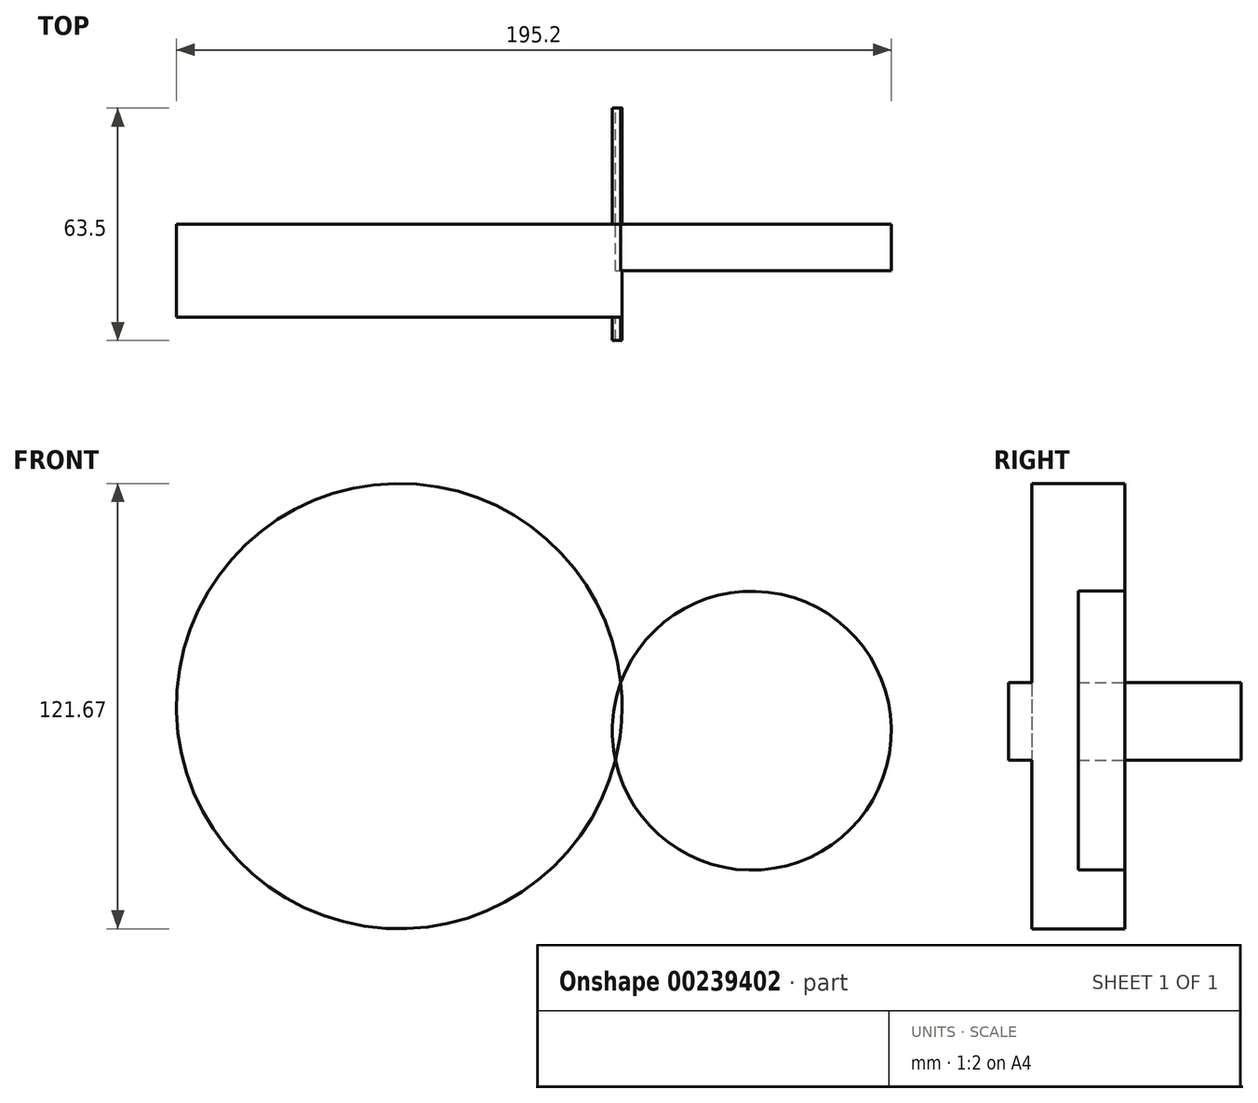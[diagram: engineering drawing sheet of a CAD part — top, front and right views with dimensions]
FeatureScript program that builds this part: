
annotation { "Feature Type Name" : "Feature", "Feature Type Description" : "" }
export const myFeature = defineFeature(function(context is Context, id is Id, definition is map)
    precondition{}
    {
        {
            var Q0;
            Q0=qCreatedBy(makeId("Front.planeOp"),FACE);
            var sketch = newSketch(context, id + "F0", { "sketchPlane" : qUnion([Q0])});
            skCircle(sketch, "E0", {"center": v(0, 0) * mm, "radius": 38.1 * mm});
            skCircle(sketch, "E1", {"center": v(-96.27, 6.71) * mm, "radius": 60.84 * mm});
            skPoint(sketch, "E1.first.point", {"position": v(-44.8, -25.72) * mm});
            skPoint(sketch, "E1.second.point", {"position": v(-73.62, 63.18) * mm});
            skPoint(sketch, "E1.third.point", {"position": v(-35.52, 10) * mm});
            skSolve(sketch);
        }
        {
            var Q0;
            {var subQ0=sQuery(id+"F0.wireOp",EDGE,"E1");var subQ1=sQuery(id+"F0.wireOp",EDGE,"E0");var subQ2=makeQuery(id+"F0.imprint","INTERSECT",VERTEX,{"disambiguationData":[OD(0.0)],"derivedFrom":[subQ1,subQ0]});Q0=makeQuery(id+"F0.imprint","IMPRINT",FACE,{"disambiguationData":[TD([[makeQuery(id+"F0.imprint","IMPRINT",EDGE,{"disambiguationData":[TD([[subQ2,1.0]])],"derivedFrom":subQ1}),-1.0]])]});}
            extrude(context, id + "F1", {"entities" : qUnion([Q0]), "depth" : 25.4 * mm});
        }
        {
            var Q0;
            {var subQ0=sQuery(id+"F0.wireOp",EDGE,"E1");var subQ1=sQuery(id+"F0.wireOp",EDGE,"E0");var subQ2=makeQuery(id+"F0.imprint","INTERSECT",VERTEX,{"disambiguationData":[OD(0.0)],"derivedFrom":[subQ1,subQ0]});Q0=makeQuery(id+"F0.imprint","IMPRINT",FACE,{"disambiguationData":[TD([[makeQuery(id+"F0.imprint","IMPRINT",EDGE,{"disambiguationData":[TD([[subQ2,1.0]])],"derivedFrom":subQ1}),1.0]])]});}
            extrude(context, id + "F2", {"entities" : qUnion([Q0]), "operationType" : NewBodyOperationType.ADD, "endBound" : BoundingType.SYMMETRIC, "depth" : 63.5 * mm});
        }
        {
            var Q0;
            {var subQ0=sQuery(id+"F0.wireOp",EDGE,"E1");var subQ1=sQuery(id+"F0.wireOp",EDGE,"E0");var subQ2=makeQuery(id+"F0.imprint","INTERSECT",VERTEX,{"disambiguationData":[OD(0.0)],"derivedFrom":[subQ1,subQ0]});Q0=makeQuery(id+"F0.imprint","IMPRINT",FACE,{"disambiguationData":[TD([[makeQuery(id+"F0.imprint","IMPRINT",EDGE,{"disambiguationData":[TD([[subQ2,-1.0]])],"derivedFrom":subQ1}),1.0]])]});}
            extrude(context, id + "F3", {"entities" : qUnion([Q0]), "operationType" : NewBodyOperationType.ADD, "depth" : 12.7 * mm});
        }
    });
